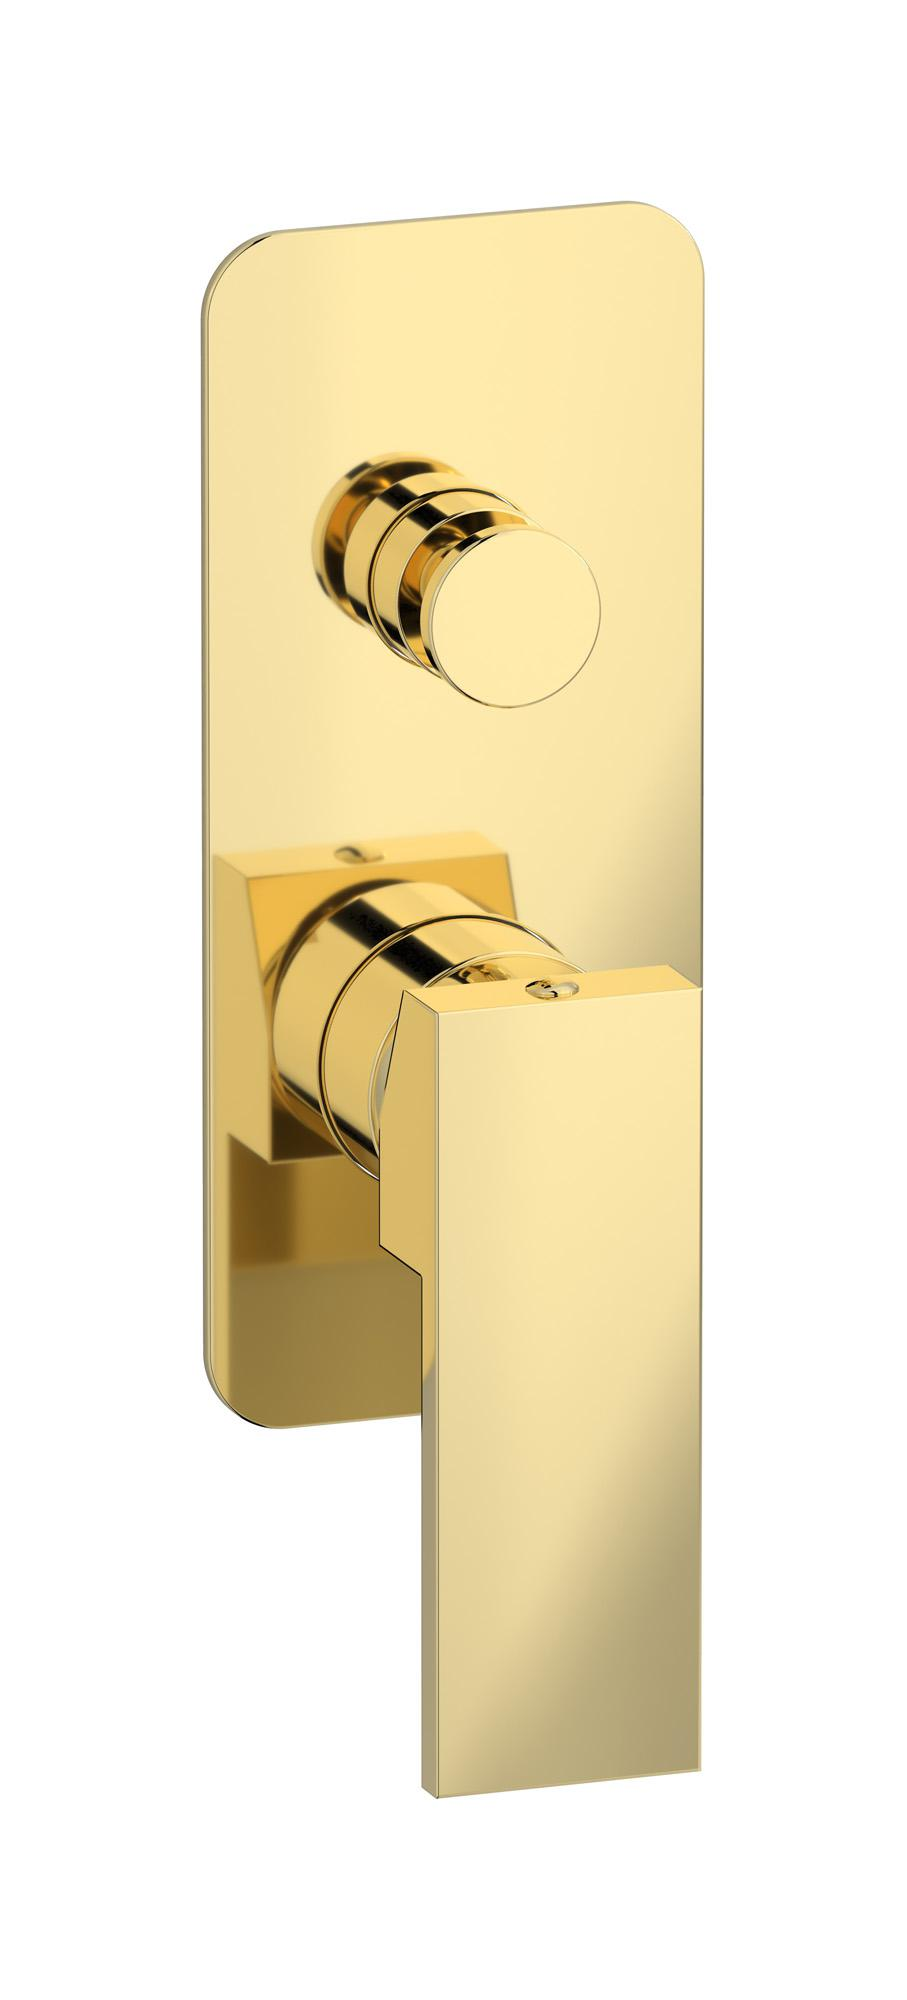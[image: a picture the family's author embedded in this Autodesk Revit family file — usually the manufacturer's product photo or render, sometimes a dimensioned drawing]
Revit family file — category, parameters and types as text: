
# Revit family: RU310
name_source: partatom
category: Apparecchi idraulici
units: mm (PartAtom-declared; Revit-internal decimal feet)

## family parameters
Basato su piano di lavoro = No
Condiviso = No
Mantieni orientamento annotazione = No
Numero OmniClass = 23.45.55.17
Punto di calcolo locali = No
Quota connettore circolare = Usa diametro
Sempre verticale = Sì
Taglio con vuoti quando caricato = No
Tipo di parte = Normale
Titolo OmniClass = Mixing Faucets

## types (12) — shared parameters
Cold water inlet = 10 mm  [stored 0.0328084 ft]
Commenti sul tipo = Exposed parts for manual wall mixer with two ways diverter
Connessione CW = No
Connessione HW = No
Connessione di scarico = No
Connessione di ventilazione = No
Descrizione = Exposed parts for manual wall mixer with two ways diverter
Hot water inlet = 10 mm  [stored 0.0328084 ft]
Produttore = IB Rubinetterie S.p.A.
URL = https://www.weareib.it
zero-valued in all types: Prospetto di default

## per-type parameters (varying)
| type | Finishes surface | Immagine tipo | Modello |
| Matt White | IB_matt white | RU310BO.jpg | RU310BO |
| Chrome | IB_Chrome | RU310CC.jpg | RU310CC |
| Black Chrome | IB_Black chrome | RU310CF.jpg | RU310CF |
| Brushed Black Chrome | IB_Brushed black chrome | RU310CS.jpg | RU310CS |
| Pale Gold | IB_Pale gold | RU310II.jpg | RU310II |
| Brushed Pale Gold | IB_brushed pale gold | RU310IS.jpg | RU310IS |
| Matt Black | IB_matt black | RU310NP.jpg | RU310NP |
| Gold | IB_gold | RU310OO.jpg | RU310OO |
| Brushed Gold | IB_brushed gold | RU310OS.jpg | RU310OS |
| Rose Gold | IB_Rose gold | RU310RS.jpg | RU310RS |
| Brushed Rose Gold | IB_Brushed rose gold | RU310SR.jpg | RU310SR |
| Brushed Nickel | IB_Brushed nickel | RU310SS.jpg | RU310SS |

note: [stored X ft] marks values corroborated as IEEE doubles in the binary element streams (Revit-internal decimal feet)
